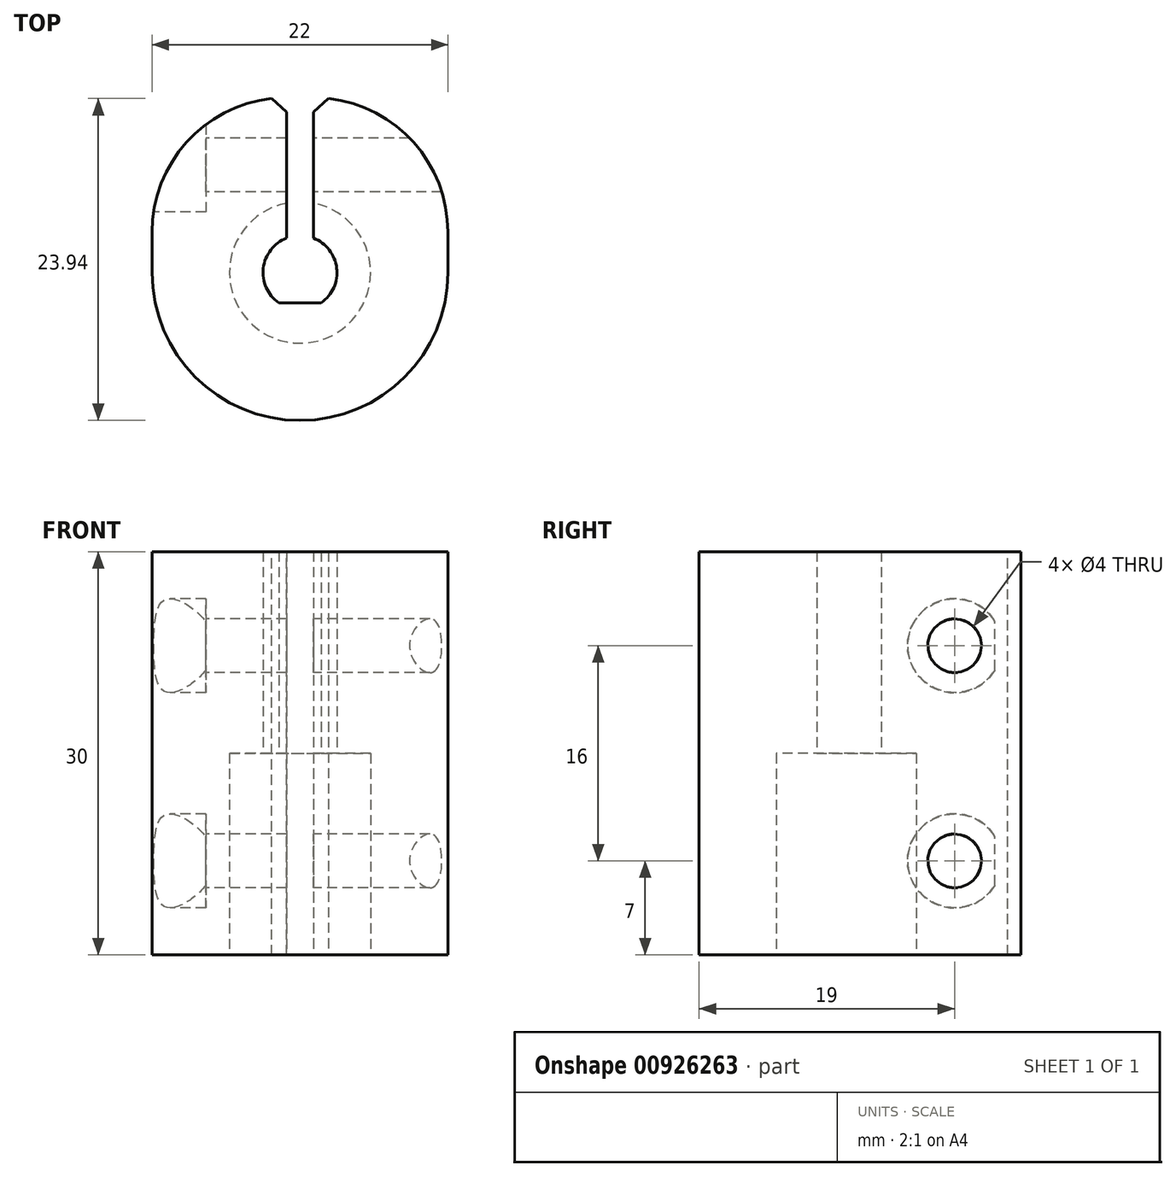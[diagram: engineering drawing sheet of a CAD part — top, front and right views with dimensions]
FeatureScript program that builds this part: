
annotation { "Feature Type Name" : "Feature", "Feature Type Description" : "" }
export const myFeature = defineFeature(function(context is Context, id is Id, definition is map)
    precondition{}
    {
        {
            var Q0;
            Q0=qCreatedBy(makeId("Top.planeOp"),FACE);
            var sketch = newSketch(context, id + "F0", { "sketchPlane" : qUnion([Q0])});
            skCircle(sketch, "E0", {"center": v(0, 0) * mm, "radius": 11 * mm});
            skCircle(sketch, "E1", {"center": v(0, 0) * mm, "radius": 5.25 * mm});
            skCircle(sketch, "E2", {"center": v(0, 0) * mm, "radius": 2.75 * mm});
            skLineSegment(sketch, "E3", {"start": v(0, 0) * mm, "end": v(0, 11) * mm, "construction": true});
            skLineSegment(sketch, "E4", {"start": v(0, 0) * mm, "end": v(11, 0) * mm, "construction": true});
            skLineSegment(sketch, "E5", {"start": v(11, 0) * mm, "end": v(11, 11) * mm});
            skLineSegment(sketch, "E6", {"start": v(11, 11) * mm, "end": v(0, 11) * mm});
            skLineSegment(sketch, "E7", {"start": v(0, 0) * mm, "end": v(-11, 0) * mm, "construction": true});
            skLineSegment(sketch, "E8", {"start": v(-11, 0) * mm, "end": v(-11, 11) * mm});
            skLineSegment(sketch, "E9", {"start": v(-11, 11) * mm, "end": v(0, 11) * mm});
            skLineSegment(sketch, "E10", {"start": v(11, 11) * mm, "end": v(11, 13) * mm});
            skLineSegment(sketch, "E11", {"start": v(11, 13) * mm, "end": v(-11, 13) * mm});
            skLineSegment(sketch, "E12", {"start": v(-11, 13) * mm, "end": v(-11, 11) * mm});
            skLineSegment(sketch, "E13", {"start": v(0, -2.25) * mm, "end": v(-1.58, -2.25) * mm});
            skLineSegment(sketch, "E14", {"start": v(0, -2.25) * mm, "end": v(1.58, -2.25) * mm});
            skLineSegment(sketch, "E15", {"start": v(0, -2.25) * mm, "end": v(0, -2.75) * mm, "construction": true});
            skSolve(sketch);
        }
        {
            var Q0;
            Q0=makeQuery(id+"F0.imprint","IMPRINT",FACE,{"disambiguationData":[TD([[makeQuery(id+"F0.imprint","IMPRINT",EDGE,{"derivedFrom":sQuery(id+"F0.wireOp",EDGE,"E0")}),1.0]])]});
            var Q1;
            Q1=makeQuery(id+"F0.imprint","IMPRINT",FACE,{"disambiguationData":[TD([[makeQuery(id+"F0.imprint","IMPRINT",EDGE,{"derivedFrom":sQuery(id+"F0.wireOp",EDGE,"E1")}),1.0]])]});
            var Q2;
            {var subQ2=sQuery(id+"F0.wireOp",EDGE,"E8");Q2=makeQuery(id+"F0.imprint","IMPRINT",FACE,{"disambiguationData":[TD([[makeQuery(id+"F0.imprint","IMPRINT",EDGE,{"derivedFrom":subQ2}),-1.0]])]});}
            var Q3;
            {var subQ0=sQuery(id+"F0.wireOp",EDGE,"E5");Q3=makeQuery(id+"F0.imprint","IMPRINT",FACE,{"disambiguationData":[TD([[makeQuery(id+"F0.imprint","IMPRINT",EDGE,{"derivedFrom":subQ0}),1.0]])]});}
            var Q4;
            Q4=makeQuery(id+"F0.imprint","IMPRINT",FACE,{"disambiguationData":[TD([[makeQuery(id+"F0.imprint","IMPRINT",EDGE,{"derivedFrom":sQuery(id+"F0.wireOp",EDGE,"E6")}),-1.0]])]});
            var Q5;
            {var subQ0=sQuery(id+"F0.wireOp",EDGE,"E13");Q5=makeQuery(id+"F0.imprint","IMPRINT",FACE,{"disambiguationData":[TD([[makeQuery(id+"F0.imprint","IMPRINT",EDGE,{"derivedFrom":subQ0}),1.0]])]});}
            var Q6;
            {var subQ0=sQuery(id+"F0.wireOp",EDGE,"E13");Q6=makeQuery(id+"F0.imprint","IMPRINT",FACE,{"disambiguationData":[TD([[makeQuery(id+"F0.imprint","IMPRINT",EDGE,{"derivedFrom":subQ0}),-1.0]])]});}
            extrude(context, id + "F1", {"entities" : qUnion([Q0, Q1, Q2, Q3, Q4, Q5, Q6]), "depth" : 30 * mm, "offsetDistance" : 25 * mm});
        }
        {
            var Q0;
            Q0=makeQuery(id+"F0.imprint","IMPRINT",FACE,{"disambiguationData":[TD([[makeQuery(id+"F0.imprint","IMPRINT",EDGE,{"derivedFrom":sQuery(id+"F0.wireOp",EDGE,"E1")}),1.0]])]});
            var Q1;
            {var subQ0=sQuery(id+"F0.wireOp",EDGE,"E13");Q1=makeQuery(id+"F0.imprint","IMPRINT",FACE,{"disambiguationData":[TD([[makeQuery(id+"F0.imprint","IMPRINT",EDGE,{"derivedFrom":subQ0}),1.0]])]});}
            extrude(context, id + "F2", {"entities" : qUnion([Q0, Q1]), "operationType" : NewBodyOperationType.REMOVE, "depth" : 15 * mm, "offsetDistance" : 25 * mm});
        }
        {
            var Q0;
            {var subQ0=sQuery(id+"F0.wireOp",EDGE,"E13");Q0=makeQuery(id+"F0.imprint","IMPRINT",FACE,{"disambiguationData":[TD([[makeQuery(id+"F0.imprint","IMPRINT",EDGE,{"derivedFrom":subQ0}),-1.0]])]});}
            extrude(context, id + "F3", {"entities" : qUnion([Q0]), "operationType" : NewBodyOperationType.REMOVE, "depth" : 30 * mm, "offsetDistance" : 25 * mm});
        }
        {
            var Q0;
            Q0=makeQuery(id+"F1.opExtrude","SWEPT_FACE",FACE,{"disambiguationData":[OSD([sQuery(id+"F0.wireOp",EDGE,"E8"),sQuery(id+"F0.wireOp",EDGE,"E12")])]});
            var sketch = newSketch(context, id + "F4", { "sketchPlane" : qUnion([Q0])});
            skLineSegment(sketch, "E16.0", {"start": v(0, 30) * mm, "end": v(0, 0) * mm});
            skLineSegment(sketch, "E16.1", {"start": v(-13, 30) * mm, "end": v(-13, 0) * mm});
            skLineSegment(sketch, "E16.4", {"start": v(0, 30) * mm, "end": v(-13, 30) * mm});
            skCircle(sketch, "E17", {"center": v(-8, 7) * mm, "radius": 2 * mm});
            skCircle(sketch, "E18", {"center": v(-8, 23) * mm, "radius": 2 * mm});
            skCircle(sketch, "E19", {"center": v(-8, 23) * mm, "radius": 3.5 * mm});
            skCircle(sketch, "E20", {"center": v(-8, 7) * mm, "radius": 3.5 * mm});
            skLineSegment(sketch, "E21", {"start": v(-13, 0) * mm, "end": v(0, 0) * mm});
            skSolve(sketch);
        }
        {
            var Q0;
            Q0=makeQuery(id+"F1.opExtrude","SWEPT_FACE",FACE,{"disambiguationData":[OSD([sQuery(id+"F0.wireOp",EDGE,"E5"),sQuery(id+"F0.wireOp",EDGE,"E10")])]});
            var sketch = newSketch(context, id + "F5", { "sketchPlane" : qUnion([Q0])});
            skLineSegment(sketch, "E22.0.3", {"start": v(13, 30) * mm, "end": v(13, 0) * mm});
            skCircle(sketch, "E22.1", {"center": v(8, 7) * mm, "radius": 2 * mm});
            skLineSegment(sketch, "E22.3.2", {"start": v(0, 0) * mm, "end": v(0, 30) * mm});
            skCircle(sketch, "E22.4.0", {"center": v(8, 7) * mm, "radius": 2 * mm});
            skPoint(sketch, "E22.6", {"position": v(8, 23) * mm});
            skCircle(sketch, "E22.7.0", {"center": v(8, 23) * mm, "radius": 2 * mm});
            skCircle(sketch, "E23.cCircle", {"center": v(8, 7) * mm, "radius": 2.85 * mm, "construction": true});
            skLineSegment(sketch, "E23.0", {"start": v(9.65, 4.15) * mm, "end": v(6.35, 4.15) * mm});
            skLineSegment(sketch, "E23.1", {"start": v(6.35, 4.15) * mm, "end": v(4.7, 7) * mm});
            skLineSegment(sketch, "E23.2", {"start": v(4.7, 7) * mm, "end": v(6.35, 9.85) * mm});
            skLineSegment(sketch, "E23.3", {"start": v(6.35, 9.85) * mm, "end": v(9.65, 9.85) * mm});
            skLineSegment(sketch, "E23.4", {"start": v(9.65, 9.85) * mm, "end": v(11.3, 7) * mm});
            skLineSegment(sketch, "E23.5", {"start": v(11.3, 7) * mm, "end": v(9.65, 4.15) * mm});
            skPoint(sketch, "E23.0.midPoint", {"position": v(8, 4.15) * mm});
            skCircle(sketch, "E24.cCircle", {"center": v(8, 23) * mm, "radius": 2.85 * mm, "construction": true});
            skLineSegment(sketch, "E24.0", {"start": v(9.65, 20.15) * mm, "end": v(6.35, 20.15) * mm});
            skLineSegment(sketch, "E24.1", {"start": v(6.35, 20.15) * mm, "end": v(4.7, 23) * mm});
            skLineSegment(sketch, "E24.2", {"start": v(4.7, 23) * mm, "end": v(6.35, 25.85) * mm});
            skLineSegment(sketch, "E24.3", {"start": v(6.35, 25.85) * mm, "end": v(9.65, 25.85) * mm});
            skLineSegment(sketch, "E24.4", {"start": v(9.65, 25.85) * mm, "end": v(11.3, 23) * mm});
            skLineSegment(sketch, "E24.5", {"start": v(11.3, 23) * mm, "end": v(9.65, 20.15) * mm});
            skPoint(sketch, "E24.0.midPoint", {"position": v(8, 20.15) * mm});
            skLineSegment(sketch, "E25", {"start": v(13, 30) * mm, "end": v(0, 30) * mm});
            skSolve(sketch);
        }
        {
            var Q0;
            Q0=makeQuery(id+"F4.imprint","IMPRINT",FACE,{"disambiguationData":[TD([[makeQuery(id+"F4.imprint","IMPRINT",EDGE,{"derivedFrom":sQuery(id+"F4.wireOp",EDGE,"E17")}),1.0]])]});
            var Q1;
            Q1=makeQuery(id+"F4.imprint","IMPRINT",FACE,{"disambiguationData":[TD([[makeQuery(id+"F4.imprint","IMPRINT",EDGE,{"derivedFrom":sQuery(id+"F4.wireOp",EDGE,"E18")}),1.0]])]});
            extrude(context, id + "F6", {"entities" : qUnion([Q0, Q1]), "operationType" : NewBodyOperationType.REMOVE, "oppositeDirection" : true, "depth" : 22 * mm, "offsetDistance" : 25 * mm});
        }
        {
            var Q0;
            Q0=makeQuery(id+"F4.imprint","IMPRINT",FACE,{"disambiguationData":[TD([[makeQuery(id+"F4.imprint","IMPRINT",EDGE,{"derivedFrom":sQuery(id+"F4.wireOp",EDGE,"E17")}),-1.0]])]});
            var Q1;
            Q1=makeQuery(id+"F4.imprint","IMPRINT",FACE,{"disambiguationData":[TD([[makeQuery(id+"F4.imprint","IMPRINT",EDGE,{"derivedFrom":sQuery(id+"F4.wireOp",EDGE,"E18")}),-1.0]])]});
            extrude(context, id + "F7", {"entities" : qUnion([Q0, Q1]), "operationType" : NewBodyOperationType.REMOVE, "oppositeDirection" : true, "depth" : 4 * mm, "offsetDistance" : 25 * mm});
        }
        {
            var Q0;
            Q0=makeQuery(id+"F5.imprint","IMPRINT",FACE,{"disambiguationData":[TD([[makeQuery(id+"F5.imprint","IMPRINT",EDGE,{"derivedFrom":sQuery(id+"F5.wireOp",EDGE,"E22.4.0")}),1.0]])]});
            var Q1;
            Q1=makeQuery(id+"F5.imprint","IMPRINT",FACE,{"disambiguationData":[TD([[makeQuery(id+"F5.imprint","IMPRINT",EDGE,{"derivedFrom":sQuery(id+"F5.wireOp",EDGE,"E22.7.0")}),1.0]])]});
            extrude(context, id + "F8", {"entities" : qUnion([Q0, Q1]), "operationType" : NewBodyOperationType.REMOVE, "oppositeDirection" : true, "depth" : 4 * mm, "offsetDistance" : 25 * mm});
        }
        {
            var Q0;
            Q0=makeQuery(id+"F1.opExtrude","SWEPT_FACE",FACE,{"disambiguationData":[OSD([sQuery(id+"F0.wireOp",EDGE,"E11")])]});
            var sketch = newSketch(context, id + "F9", { "sketchPlane" : qUnion([Q0])});
            skLineSegment(sketch, "E26.0", {"start": v(11, 30) * mm, "end": v(11, 0) * mm});
            skLineSegment(sketch, "E26.1", {"start": v(-11, 0) * mm, "end": v(11, 0) * mm});
            skLineSegment(sketch, "E26.2", {"start": v(-11, 30) * mm, "end": v(-11, 0) * mm});
            skLineSegment(sketch, "E26.3", {"start": v(-11, 30) * mm, "end": v(11, 30) * mm});
            skLineSegment(sketch, "E27", {"start": v(0, 0) * mm, "end": v(0, 30) * mm});
            skLineSegment(sketch, "E28", {"start": v(-1, 30) * mm, "end": v(-1, 0) * mm});
            skLineSegment(sketch, "E29", {"start": v(1, 0) * mm, "end": v(1, 30) * mm});
            skSolve(sketch);
        }
        {
            var Q0;
            {var subQ0=sQuery(id+"F9.wireOp",EDGE,"E27");Q0=makeQuery(id+"F9.imprint","IMPRINT",FACE,{"disambiguationData":[TD([[makeQuery(id+"F9.imprint","IMPRINT",EDGE,{"derivedFrom":subQ0}),-1.0]])]});}
            var Q1;
            {var subQ0=sQuery(id+"F9.wireOp",EDGE,"E27");Q1=makeQuery(id+"F9.imprint","IMPRINT",FACE,{"disambiguationData":[TD([[makeQuery(id+"F9.imprint","IMPRINT",EDGE,{"derivedFrom":subQ0}),1.0]])]});}
            extrude(context, id + "F10", {"entities" : qUnion([Q0, Q1]), "operationType" : NewBodyOperationType.REMOVE, "oppositeDirection" : true, "depth" : 15 * mm, "offsetDistance" : 25 * mm});
        }
        {
            var Q0;
            Q0=makeQuery(id+"F1.opExtrude","SWEPT_EDGE",EDGE,{"disambiguationData":[OSD([sQuery(id+"F0.wireOp",EDGE,"E11"),sQuery(id+"F0.wireOp",EDGE,"E12")])]});
            var Q1;
            Q1=makeQuery(id+"F1.opExtrude","SWEPT_EDGE",EDGE,{"disambiguationData":[OSD([sQuery(id+"F0.wireOp",EDGE,"E10"),sQuery(id+"F0.wireOp",EDGE,"E11")])]});
            fillet(context, id + "F11", {"entities" : qUnion([Q0, Q1]), "radius" : 10 * mm, "tangentPropagation" : true, "allowEdgeOverflow" : false});
        }
        {
            var Q0;
            Q0=makeQuery(id+"F11.opFillet","BLEND_EDGE",EDGE,{"blendedFrom":[makeQuery(id+"F1.opExtrude","SWEPT_EDGE",EDGE,{"disambiguationData":[OSD([sQuery(id+"F0.wireOp",EDGE,"E11"),sQuery(id+"F0.wireOp",EDGE,"E12")])]}),makeQuery(id+"F10.boolean.opBoolean","COPY",FACE,{"derivedFrom":makeQuery(id+"F10.opExtrude","SWEPT_FACE",FACE,{"disambiguationData":[OSD([sQuery(id+"F9.wireOp",EDGE,"E29")])]})})],"blendedInto":[makeQuery(id+"F10.boolean.opBoolean","COPY",FACE,{"derivedFrom":makeQuery(id+"F10.opExtrude","SWEPT_FACE",FACE,{"disambiguationData":[OSD([sQuery(id+"F9.wireOp",EDGE,"E29")])]})})]});
            var Q1;
            Q1=makeQuery(id+"F11.opFillet","BLEND_EDGE",EDGE,{"blendedFrom":[makeQuery(id+"F1.opExtrude","SWEPT_EDGE",EDGE,{"disambiguationData":[OSD([sQuery(id+"F0.wireOp",EDGE,"E10"),sQuery(id+"F0.wireOp",EDGE,"E11")])]}),makeQuery(id+"F10.boolean.opBoolean","COPY",FACE,{"derivedFrom":makeQuery(id+"F10.opExtrude","SWEPT_FACE",FACE,{"disambiguationData":[OSD([sQuery(id+"F9.wireOp",EDGE,"E28")])]})})],"blendedInto":[makeQuery(id+"F10.boolean.opBoolean","COPY",FACE,{"derivedFrom":makeQuery(id+"F10.opExtrude","SWEPT_FACE",FACE,{"disambiguationData":[OSD([sQuery(id+"F9.wireOp",EDGE,"E28")])]})})]});
            chamfer(context, id + "F12", {"entities" : qUnion([Q0, Q1]), "width" : 1 * mm});
        }
    });
